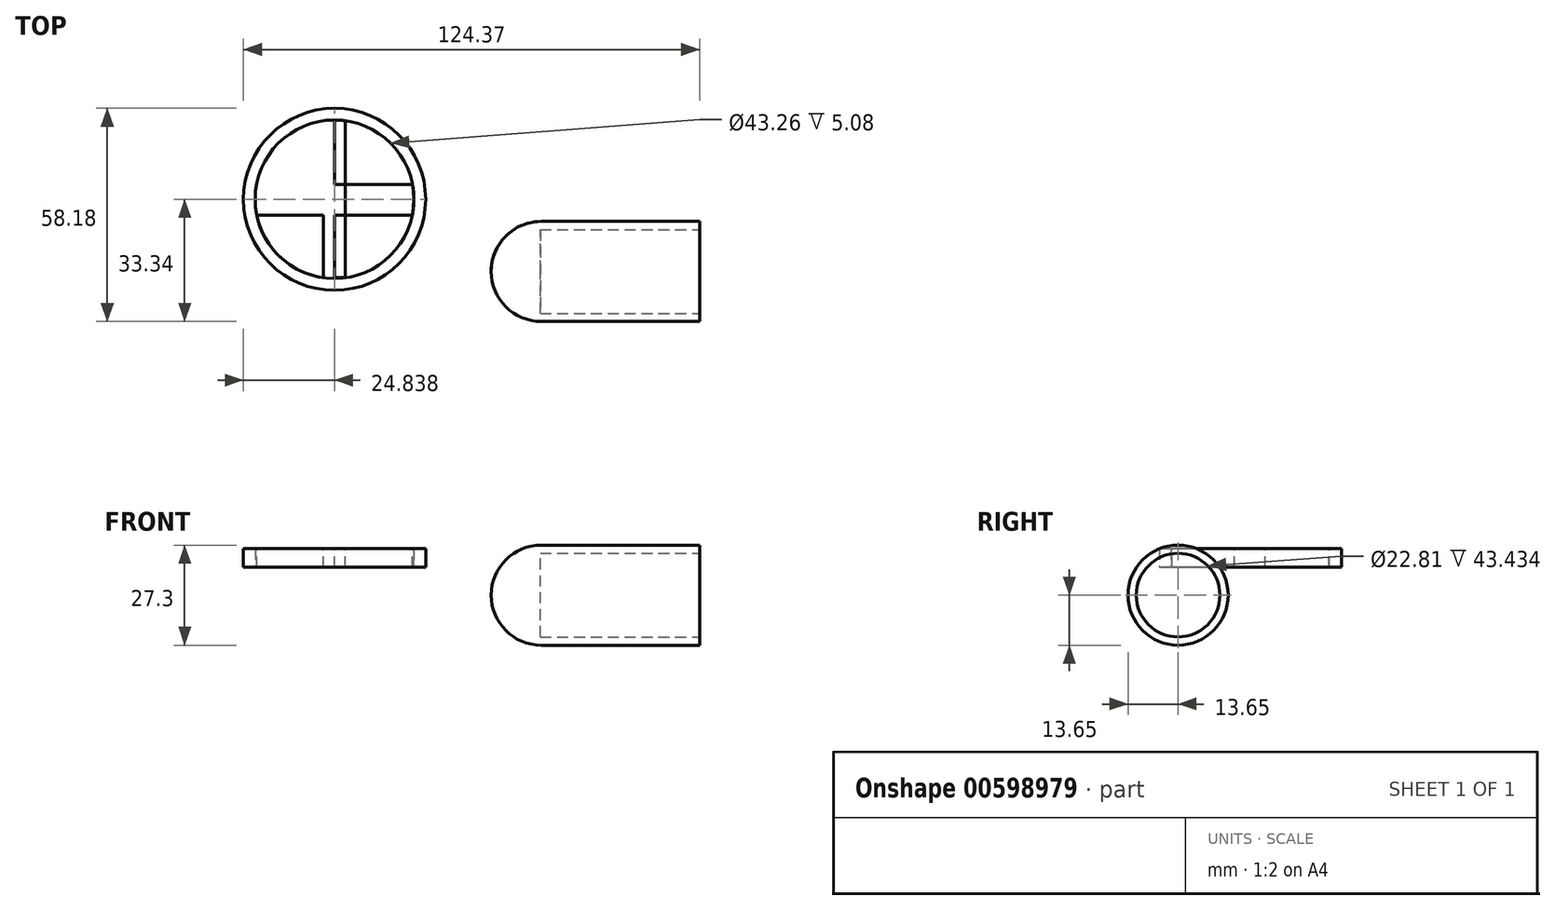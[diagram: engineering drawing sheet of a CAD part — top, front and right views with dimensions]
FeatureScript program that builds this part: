
annotation { "Feature Type Name" : "Feature", "Feature Type Description" : "" }
export const myFeature = defineFeature(function(context is Context, id is Id, definition is map)
    precondition{}
    {
        {
            var Q0;
            Q0=qCreatedBy(makeId("Right.planeOp"),FACE);
            var sketch = newSketch(context, id + "F0", { "sketchPlane" : qUnion([Q0])});
            skCircle(sketch, "E0", {"center": v(0, 0) * mm, "radius": 13.65 * mm});
            skSolve(sketch);
        }
        {
            var Q0;
            Q0 = qSketchRegion(id + "F0", true);
            extrude(context, id + "F1", {"entities" : qUnion([Q0]), "depth" : 43.18 * mm, "offsetDistance" : 25.4 * mm});
        }
        {
            var Q0;
            Q0=qCreatedBy(makeId("Top.planeOp"),FACE);
            var sketch = newSketch(context, id + "F2", { "sketchPlane" : qUnion([Q0])});
            skLineSegment(sketch, "E1", {"start": v(0, 13.65) * mm, "end": v(43.18, 13.65) * mm});
            skArc(sketch, "E2", {"start": v(0, 13.65) * mm, "mid": v(-9.65, 9.65) * mm, "end": v(-13.65, 0) * mm});
            skLineSegment(sketch, "E3", {"start": v(0, 13.65) * mm, "end": v(0, 0) * mm});
            skLineSegment(sketch, "E4", {"start": v(0, 0) * mm, "end": v(-13.65, 0) * mm});
            skSolve(sketch);
        }
        {
            var Q0;
            Q0=makeQuery(id+"F2.imprint","IMPRINT",FACE,{"disambiguationData":[TD([[makeQuery(id+"F2.imprint","IMPRINT",EDGE,{"derivedFrom":sQuery(id+"F2.wireOp",EDGE,"E2")}),1.0]])]});
            var Q1;
            Q1=sQuery(id+"F2.wireOp",EDGE,"E4");
            revolve(context, id + "F3", {"operationType" : NewBodyOperationType.ADD, "entities" : qUnion([Q0]), "axis" : qUnion([Q1]), "revolveType" : RevolveType.FULL});
        }
        {
            var Q0;
            Q0=makeQuery(id+"F1.opExtrude","CAP_FACE",FACE,{"disambiguationData":[OSD([sQuery(id+"F0.wireOp",EDGE,"E0")])],"isStart":false});
            var sketch = newSketch(context, id + "F4", { "sketchPlane" : qUnion([Q0])});
            skCircle(sketch, "E5", {"center": v(0, 0) * mm, "radius": 11.4 * mm});
            skSolve(sketch);
        }
        {
            var Q0;
            Q0=makeQuery(id+"F4.imprint","IMPRINT",FACE,{"disambiguationData":[TD([[makeQuery(id+"F4.imprint","IMPRINT",EDGE,{"derivedFrom":sQuery(id+"F4.wireOp",EDGE,"E5")}),1.0]])]});
            extrude(context, id + "F5", {"entities" : qUnion([Q0]), "operationType" : NewBodyOperationType.REMOVE, "oppositeDirection" : true, "depth" : 43.43 * mm, "offsetDistance" : 25.4 * mm});
        }
        {
            var Q0;
            Q0=qCreatedBy(makeId("Top.planeOp"),FACE);
            var sketch = newSketch(context, id + "F6", { "sketchPlane" : qUnion([Q0])});
            skCircle(sketch, "E6", {"center": v(-56.35, 19.69) * mm, "radius": 24.84 * mm});
            skCircle(sketch, "E7", {"center": v(-56.35, 19.69) * mm, "radius": 21.63 * mm});
            skCircle(sketch, "E8", {"center": v(-56.35, 19.69) * mm, "radius": 3.88 * mm});
            skSolve(sketch);
        }
        {
            var Q0;
            Q0=makeQuery(id+"F6.imprint","IMPRINT",FACE,{"disambiguationData":[TD([[makeQuery(id+"F6.imprint","IMPRINT",EDGE,{"derivedFrom":sQuery(id+"F6.wireOp",EDGE,"E6")}),1.0]])]});
            extrude(context, id + "F7", {"entities" : qUnion([Q0]), "depth" : 12.7 * mm, "offsetDistance" : 25.4 * mm});
        }
        {
            var Q0;
            Q0=makeQuery(id+"F7.opExtrude","CAP_FACE",FACE,{"disambiguationData":[OSD([sQuery(id+"F6.wireOp",EDGE,"E6"),sQuery(id+"F6.wireOp",EDGE,"E7")])],"isStart":false});
            var sketch = newSketch(context, id + "F8", { "sketchPlane" : qUnion([Q0])});
            skLineSegment(sketch, "E9", {"start": v(-56.35, 19.69) * mm, "end": v(-56.35, 41.32) * mm});
            skLineSegment(sketch, "E10", {"start": v(-56.35, 41.32) * mm, "end": v(-56.35, -1.94) * mm});
            skLineSegment(sketch, "E11", {"start": v(-56.35, 19.69) * mm, "end": v(-77.98, 19.69) * mm});
            skLineSegment(sketch, "E12", {"start": v(-77.98, 19.69) * mm, "end": v(-34.72, 19.69) * mm});
            skLineSegment(sketch, "E13.bottom", {"start": v(-56.35, 41.32) * mm, "end": v(-59.45, 41.32) * mm});
            skLineSegment(sketch, "E13.top", {"start": v(-56.35, -1.72) * mm, "end": v(-59.45, -1.72) * mm});
            skLineSegment(sketch, "E13.left", {"start": v(-56.35, 41.32) * mm, "end": v(-56.35, -1.72) * mm});
            skLineSegment(sketch, "E13.right", {"start": v(-59.45, 41.32) * mm, "end": v(-59.45, -1.72) * mm});
            skLineSegment(sketch, "E14.bottom", {"start": v(-59.45, -1.72) * mm, "end": v(-53.4, -1.72) * mm});
            skLineSegment(sketch, "E14.top", {"start": v(-59.45, 41.32) * mm, "end": v(-53.4, 41.32) * mm});
            skLineSegment(sketch, "E14.left", {"start": v(-59.45, -1.72) * mm, "end": v(-59.45, 41.32) * mm});
            skLineSegment(sketch, "E14.right", {"start": v(-53.4, -1.72) * mm, "end": v(-53.4, 41.32) * mm});
            skLineSegment(sketch, "E15.bottom", {"start": v(-35.11, 23.77) * mm, "end": v(-77.54, 23.77) * mm});
            skLineSegment(sketch, "E15.top", {"start": v(-35.11, 15.34) * mm, "end": v(-77.54, 15.34) * mm});
            skLineSegment(sketch, "E15.left", {"start": v(-35.11, 23.77) * mm, "end": v(-35.11, 15.34) * mm});
            skLineSegment(sketch, "E15.right", {"start": v(-77.54, 23.77) * mm, "end": v(-77.54, 15.34) * mm});
            skSolve(sketch);
        }
        {
            var Q0;
            {var subQ3=sQuery(id+"F8.wireOp",EDGE,"E15.bottom");var subQ5=sQuery(id+"F8.wireOp",EDGE,"E14.left");var subQ6=makeQuery(id+"F8.imprint","INTERSECT",VERTEX,{"derivedFrom":[subQ5,subQ3]});Q0=makeQuery(id+"F8.imprint","IMPRINT",FACE,{"disambiguationData":[TD([[makeQuery(id+"F8.imprint","IMPRINT",EDGE,{"disambiguationData":[TD([[subQ6,-1.0]])],"derivedFrom":subQ5}),-1.0]])]});}
            var Q1;
            {var subQ3=sQuery(id+"F8.wireOp",EDGE,"E15.bottom");var subQ5=sQuery(id+"F8.wireOp",EDGE,"E14.right");var subQ6=makeQuery(id+"F8.imprint","INTERSECT",VERTEX,{"derivedFrom":[subQ5,subQ3]});Q1=makeQuery(id+"F8.imprint","IMPRINT",FACE,{"disambiguationData":[TD([[makeQuery(id+"F8.imprint","IMPRINT",EDGE,{"disambiguationData":[TD([[subQ6,-1.0]])],"derivedFrom":subQ5}),1.0]])]});}
            var Q2;
            {var subQ0=sQuery(id+"F8.wireOp",EDGE,"E15.right");var subQ1=sQuery(id+"F8.wireOp",EDGE,"E12");var subQ2=makeQuery(id+"F8.imprint","INTERSECT",VERTEX,{"derivedFrom":[subQ1,subQ0]});Q2=makeQuery(id+"F8.imprint","IMPRINT",FACE,{"disambiguationData":[TD([[makeQuery(id+"F8.imprint","IMPRINT",EDGE,{"disambiguationData":[TD([[subQ2,-1.0]])],"derivedFrom":subQ1}),1.0]])]});}
            var Q3;
            {var subQ0=sQuery(id+"F8.wireOp",EDGE,"E15.right");var subQ1=sQuery(id+"F8.wireOp",EDGE,"E12");var subQ2=makeQuery(id+"F8.imprint","INTERSECT",VERTEX,{"derivedFrom":[subQ1,subQ0]});Q3=makeQuery(id+"F8.imprint","IMPRINT",FACE,{"disambiguationData":[TD([[makeQuery(id+"F8.imprint","IMPRINT",EDGE,{"disambiguationData":[TD([[subQ2,-1.0]])],"derivedFrom":subQ1}),-1.0]])]});}
            var Q4;
            {var subQ0=sQuery(id+"F8.wireOp",EDGE,"E14.right");var subQ1=sQuery(id+"F8.wireOp",EDGE,"E12");var subQ2=makeQuery(id+"F8.imprint","INTERSECT",VERTEX,{"derivedFrom":[subQ1,subQ0]});Q4=makeQuery(id+"F8.imprint","IMPRINT",FACE,{"disambiguationData":[TD([[makeQuery(id+"F8.imprint","IMPRINT",EDGE,{"disambiguationData":[TD([[subQ2,-1.0]])],"derivedFrom":subQ1}),-1.0]])]});}
            var Q5;
            {var subQ0=sQuery(id+"F8.wireOp",EDGE,"E14.right");var subQ1=sQuery(id+"F8.wireOp",EDGE,"E12");var subQ2=makeQuery(id+"F8.imprint","INTERSECT",VERTEX,{"derivedFrom":[subQ1,subQ0]});Q5=makeQuery(id+"F8.imprint","IMPRINT",FACE,{"disambiguationData":[TD([[makeQuery(id+"F8.imprint","IMPRINT",EDGE,{"disambiguationData":[TD([[subQ2,-1.0]])],"derivedFrom":subQ1}),1.0]])]});}
            var Q6;
            {var subQ0=sQuery(id+"F8.wireOp",EDGE,"E14.bottom");var subQ5=sQuery(id+"F8.wireOp",EDGE,"E14.right");var subQ6=makeQuery(id+"F8.imprint","INTERSECT",VERTEX,{"derivedFrom":[subQ0,subQ5]});Q6=makeQuery(id+"F8.imprint","IMPRINT",FACE,{"disambiguationData":[TD([[makeQuery(id+"F8.imprint","IMPRINT",EDGE,{"disambiguationData":[TD([[subQ6,-1.0]])],"derivedFrom":subQ5}),1.0]])]});}
            var Q7;
            {var subQ1=sQuery(id+"F8.wireOp",EDGE,"E13.left");var subQ3=sQuery(id+"F8.wireOp",EDGE,"E15.top");var subQ4=makeQuery(id+"F8.imprint","INTERSECT",VERTEX,{"derivedFrom":[subQ1,subQ3]});Q7=makeQuery(id+"F8.imprint","IMPRINT",FACE,{"disambiguationData":[TD([[makeQuery(id+"F8.imprint","IMPRINT",EDGE,{"disambiguationData":[TD([[subQ4,-1.0]])],"derivedFrom":subQ3}),1.0]])]});}
            extrude(context, id + "F9", {"entities" : qUnion([Q0, Q1, Q2, Q3, Q4, Q5, Q6, Q7]), "oppositeDirection" : true, "depth" : 5.08 * mm, "offsetDistance" : 25.4 * mm});
        }
        {
            var Q0;
            Q0=makeQuery(id+"F7.opExtrude","CAP_FACE",FACE,{"disambiguationData":[OSD([sQuery(id+"F6.wireOp",EDGE,"E6"),sQuery(id+"F6.wireOp",EDGE,"E7")])],"isStart":true});
            extrude(context, id + "F10", {"entities" : qUnion([Q0]), "operationType" : NewBodyOperationType.REMOVE, "oppositeDirection" : true, "depth" : 7.62 * mm, "offsetDistance" : 25.4 * mm});
        }
    });
